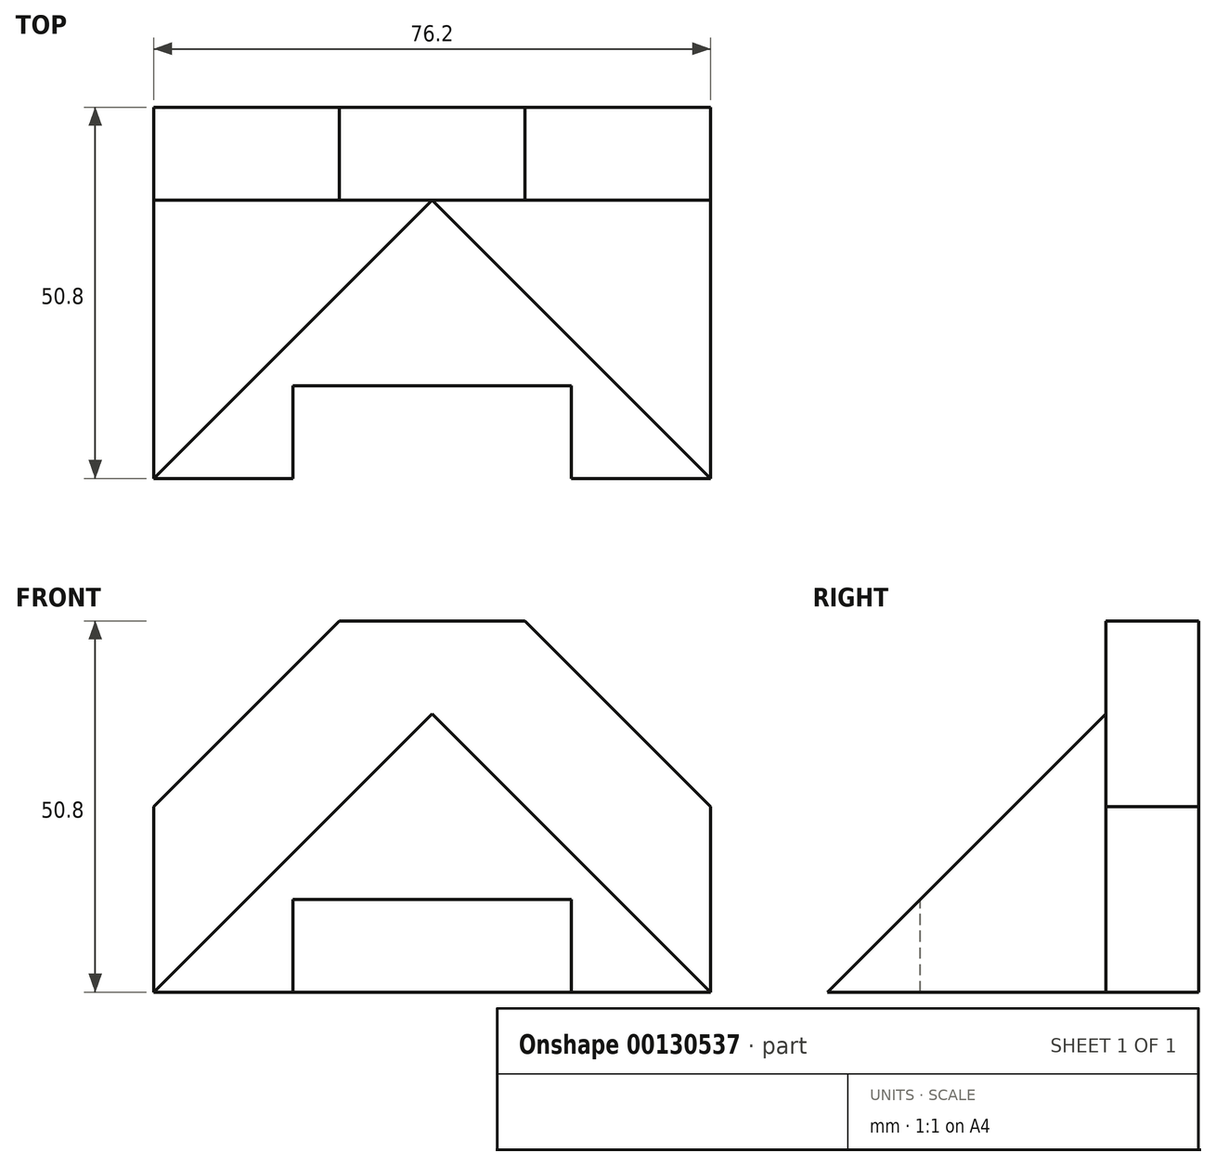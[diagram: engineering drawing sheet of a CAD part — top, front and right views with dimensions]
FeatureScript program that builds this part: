
annotation { "Feature Type Name" : "Feature", "Feature Type Description" : "" }
export const myFeature = defineFeature(function(context is Context, id is Id, definition is map)
    precondition{}
    {
        {
            var Q0;
            Q0=qCreatedBy(makeId("Front.planeOp"),FACE);
            var sketch = newSketch(context, id + "F0", { "sketchPlane" : qUnion([Q0])});
            skLineSegment(sketch, "E0", {"start": v(0, 0) * mm, "end": v(-76.2, 0) * mm});
            skLineSegment(sketch, "E1", {"start": v(-76.2, 0) * mm, "end": v(-76.2, 25.4) * mm});
            skLineSegment(sketch, "E2", {"start": v(-76.2, 25.4) * mm, "end": v(-50.8, 50.8) * mm});
            skLineSegment(sketch, "E3", {"start": v(-50.8, 50.8) * mm, "end": v(-25.4, 50.8) * mm});
            skLineSegment(sketch, "E4", {"start": v(-25.4, 50.8) * mm, "end": v(0, 25.4) * mm});
            skLineSegment(sketch, "E5", {"start": v(0, 25.4) * mm, "end": v(0, 0) * mm});
            skSolve(sketch);
        }
        {
            var Q0;
            Q0 = qSketchRegion(id + "F0", true);
            extrude(context, id + "F1", {"entities" : qUnion([Q0]), "oppositeDirection" : true, "depth" : 50.8 * mm});
        }
        {
            var Q0;
            Q0=makeQuery(id+"F1.opExtrude","CAP_FACE",FACE,{"disambiguationData":[OSD([sQuery(id+"F0.wireOp",EDGE,"E0"),sQuery(id+"F0.wireOp",EDGE,"E1"),sQuery(id+"F0.wireOp",EDGE,"E2"),sQuery(id+"F0.wireOp",EDGE,"E3"),sQuery(id+"F0.wireOp",EDGE,"E4"),sQuery(id+"F0.wireOp",EDGE,"E5")])],"isStart":true});
            var sketch = newSketch(context, id + "F2", { "sketchPlane" : qUnion([Q0])});
            skLineSegment(sketch, "E6", {"start": v(-63.5, 38.1) * mm, "end": v(-12.7, 38.1) * mm});
            skLineSegment(sketch, "E7", {"start": v(-12.7, 38.1) * mm, "end": v(-25.4, 50.8) * mm});
            skLineSegment(sketch, "E8", {"start": v(-25.4, 50.8) * mm, "end": v(-50.8, 50.8) * mm});
            skLineSegment(sketch, "E9", {"start": v(-50.8, 50.8) * mm, "end": v(-63.5, 38.1) * mm});
            skSolve(sketch);
        }
        {
            var Q0;
            Q0 = qSketchRegion(id + "F2", true);
            extrude(context, id + "F3", {"entities" : qUnion([Q0]), "operationType" : NewBodyOperationType.REMOVE, "oppositeDirection" : true, "depth" : 38.1 * mm});
        }
        {
            var Q0;
            Q0=makeQuery(id+"F3.boolean.opBoolean","COPY",FACE,{"derivedFrom":makeQuery(id+"F3.opExtrude","SWEPT_FACE",FACE,{"disambiguationData":[OSD([sQuery(id+"F2.wireOp",EDGE,"E6")])]})});
            var sketch = newSketch(context, id + "F4", { "sketchPlane" : qUnion([Q0])});
            skLineSegment(sketch, "E10", {"start": v(-19.05, 0) * mm, "end": v(-19.05, 12.7) * mm});
            skLineSegment(sketch, "E11", {"start": v(-19.05, 12.7) * mm, "end": v(-57.15, 12.7) * mm});
            skLineSegment(sketch, "E12", {"start": v(-57.15, 12.7) * mm, "end": v(-57.15, 0) * mm});
            skLineSegment(sketch, "E13", {"start": v(-57.15, 0) * mm, "end": v(-19.05, 0) * mm});
            skSolve(sketch);
        }
        {
            var Q0;
            Q0 = qSketchRegion(id + "F4", true);
            extrude(context, id + "F5", {"entities" : qUnion([Q0]), "operationType" : NewBodyOperationType.REMOVE, "endBound" : BoundingType.THROUGH_ALL, "oppositeDirection" : true, "depth" : 25.4 * mm});
        }
        {
            var Q0;
            Q0=makeQuery(id+"F1.opExtrude","SWEPT_FACE",FACE,{"disambiguationData":[OSD([sQuery(id+"F0.wireOp",EDGE,"E5")])]});
            var sketch = newSketch(context, id + "F6", { "sketchPlane" : qUnion([Q0])});
            skLineSegment(sketch, "E14", {"start": v(0, 0) * mm, "end": v(38.1, 38.1) * mm});
            skLineSegment(sketch, "E15", {"start": v(38.1, 38.1) * mm, "end": v(0, 38.1) * mm});
            skLineSegment(sketch, "E16", {"start": v(0, 38.1) * mm, "end": v(0, 0) * mm});
            skSolve(sketch);
        }
        {
            var Q0;
            Q0 = qSketchRegion(id + "F6", true);
            extrude(context, id + "F7", {"entities" : qUnion([Q0]), "operationType" : NewBodyOperationType.REMOVE, "endBound" : BoundingType.THROUGH_ALL, "oppositeDirection" : true, "depth" : 25.4 * mm});
        }
        {
            var Q0;
            Q0=makeQuery(id+"F3.boolean.opBoolean","COPY",FACE,{"derivedFrom":makeQuery(id+"F3.opExtrude","CAP_FACE",FACE,{"disambiguationData":[OSD([sQuery(id+"F2.wireOp",EDGE,"E6"),sQuery(id+"F2.wireOp",EDGE,"E7"),sQuery(id+"F2.wireOp",EDGE,"E8"),sQuery(id+"F2.wireOp",EDGE,"E9")])],"isStart":false})});
            var sketch = newSketch(context, id + "F8", { "sketchPlane" : qUnion([Q0])});
            skLineSegment(sketch, "E17", {"start": v(-38.1, 38.1) * mm, "end": v(0, 0) * mm});
            skLineSegment(sketch, "E18", {"start": v(0, 0) * mm, "end": v(0, 25.4) * mm});
            skLineSegment(sketch, "E19", {"start": v(0, 25.4) * mm, "end": v(-12.7, 38.1) * mm});
            skLineSegment(sketch, "E20", {"start": v(-12.7, 38.1) * mm, "end": v(-38.1, 38.1) * mm});
            skSolve(sketch);
        }
        {
            var Q0;
            Q0 = qSketchRegion(id + "F8", true);
            extrude(context, id + "F9", {"entities" : qUnion([Q0]), "operationType" : NewBodyOperationType.REMOVE, "endBound" : BoundingType.UP_TO_NEXT, "depth" : 25.4 * mm});
        }
        {
            var Q0;
            Q0=makeQuery(id+"F9.boolean.opBoolean","MERGE",FACE,{"derivedFrom":[makeQuery(id+"F3.boolean.opBoolean","COPY",FACE,{"derivedFrom":makeQuery(id+"F3.opExtrude","CAP_FACE",FACE,{"disambiguationData":[OSD([sQuery(id+"F2.wireOp",EDGE,"E6"),sQuery(id+"F2.wireOp",EDGE,"E7"),sQuery(id+"F2.wireOp",EDGE,"E8"),sQuery(id+"F2.wireOp",EDGE,"E9")])],"isStart":false})}),makeQuery(id+"F9.opExtrude","CAP_FACE",FACE,{"disambiguationData":[OSD([sQuery(id+"F8.wireOp",EDGE,"E17"),sQuery(id+"F8.wireOp",EDGE,"E18"),sQuery(id+"F8.wireOp",EDGE,"E19"),sQuery(id+"F8.wireOp",EDGE,"E20")])],"isStart":true})]});
            var sketch = newSketch(context, id + "F10", { "sketchPlane" : qUnion([Q0])});
            skLineSegment(sketch, "E21", {"start": v(-38.1, 38.1) * mm, "end": v(-76.2, 0) * mm});
            skLineSegment(sketch, "E22", {"start": v(-76.2, 0) * mm, "end": v(-76.2, 25.4) * mm});
            skLineSegment(sketch, "E23", {"start": v(-76.2, 25.4) * mm, "end": v(-63.5, 38.1) * mm});
            skLineSegment(sketch, "E24", {"start": v(-63.5, 38.1) * mm, "end": v(-38.1, 38.1) * mm});
            skSolve(sketch);
        }
        {
            var Q0;
            Q0 = qSketchRegion(id + "F10", true);
            extrude(context, id + "F11", {"entities" : qUnion([Q0]), "operationType" : NewBodyOperationType.REMOVE, "endBound" : BoundingType.UP_TO_NEXT, "depth" : 25.4 * mm});
        }
    });
